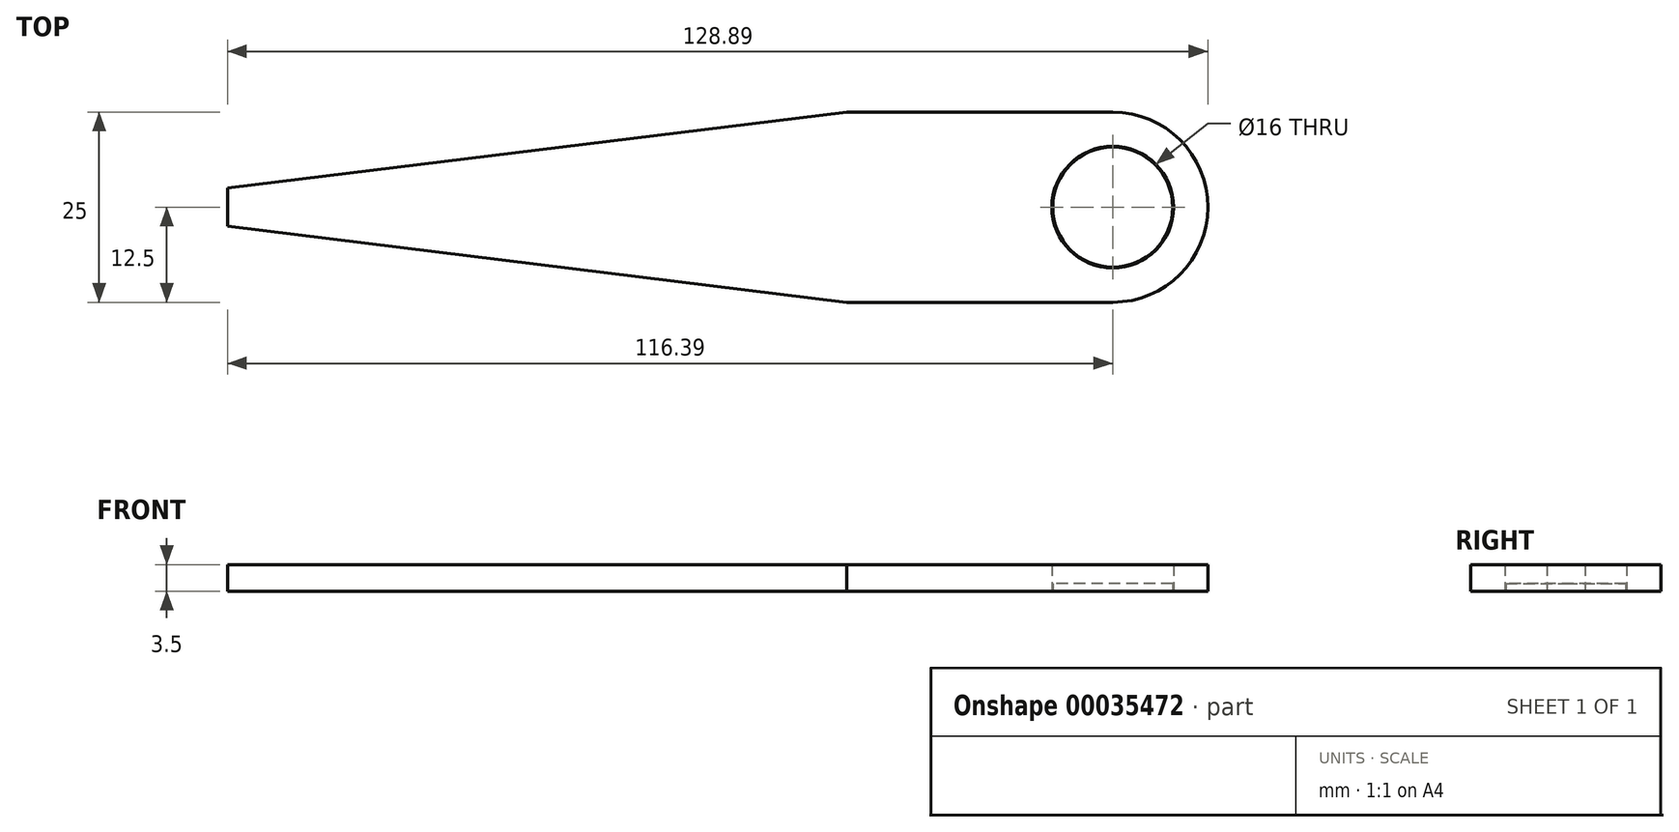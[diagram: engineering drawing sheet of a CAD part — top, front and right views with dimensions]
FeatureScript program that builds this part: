
annotation { "Feature Type Name" : "Feature", "Feature Type Description" : "" }
export const myFeature = defineFeature(function(context is Context, id is Id, definition is map)
    precondition{}
    {
        {
            var Q0;
            Q0=qCreatedBy(makeId("Top.planeOp"),FACE);
            var sketch = newSketch(context, id + "F0", { "sketchPlane" : qUnion([Q0])});
            skCircle(sketch, "E0", {"center": v(0, 0) * mm, "radius": 8 * mm});
            skCircle(sketch, "E1", {"center": v(0, 0) * mm, "radius": 12.5 * mm});
            skLineSegment(sketch, "E2", {"start": v(-35, 12.5) * mm, "end": v(0, 12.5) * mm});
            skLineSegment(sketch, "E3", {"start": v(-35, -12.5) * mm, "end": v(0, -12.5) * mm});
            skLineSegment(sketch, "E4", {"start": v(-35, 12.5) * mm, "end": v(-94.33, 12.5) * mm, "construction": true});
            skLineSegment(sketch, "E5", {"start": v(-35, 12.5) * mm, "end": v(-116.39, 2.5) * mm});
            skLineSegment(sketch, "E6", {"start": v(-35, -12.5) * mm, "end": v(-116.6, -12.5) * mm, "construction": true});
            skLineSegment(sketch, "E7", {"start": v(-35, -12.5) * mm, "end": v(-116.39, -2.5) * mm});
            skLineSegment(sketch, "E8", {"start": v(-116.39, 2.5) * mm, "end": v(-116.39, -2.5) * mm});
            skSolve(sketch);
        }
        {
            var Q0;
            {var subQ1=sQuery(id+"F0.wireOp",EDGE,"E2");Q0=makeQuery(id+"F0.imprint","IMPRINT",FACE,{"disambiguationData":[TD([[makeQuery(id+"F0.imprint","IMPRINT",EDGE,{"derivedFrom":subQ1}),-1.0]])]});}
            var Q1;
            Q1=makeQuery(id+"F0.imprint","IMPRINT",FACE,{"disambiguationData":[TD([[makeQuery(id+"F0.imprint","IMPRINT",EDGE,{"derivedFrom":sQuery(id+"F0.wireOp",EDGE,"E0")}),-1.0]])]});
            extrude(context, id + "F1", {"entities" : qUnion([Q0, Q1]), "depth" : 3.5 * mm});
        }
        {
            var Q0;
            Q0=qCreatedBy(makeId("Top.planeOp"),FACE);
            var sketch = newSketch(context, id + "F2", { "sketchPlane" : qUnion([Q0])});
            skCircle(sketch, "E9", {"center": v(0, 0) * mm, "radius": 7.9 * mm});
            skSolve(sketch);
        }
        {
            var Q0;
            Q0 = qSketchRegion(id + "F2", true);
            extrude(context, id + "F3", {"entities" : qUnion([Q0]), "depth" : 1 * mm});
        }
    });
